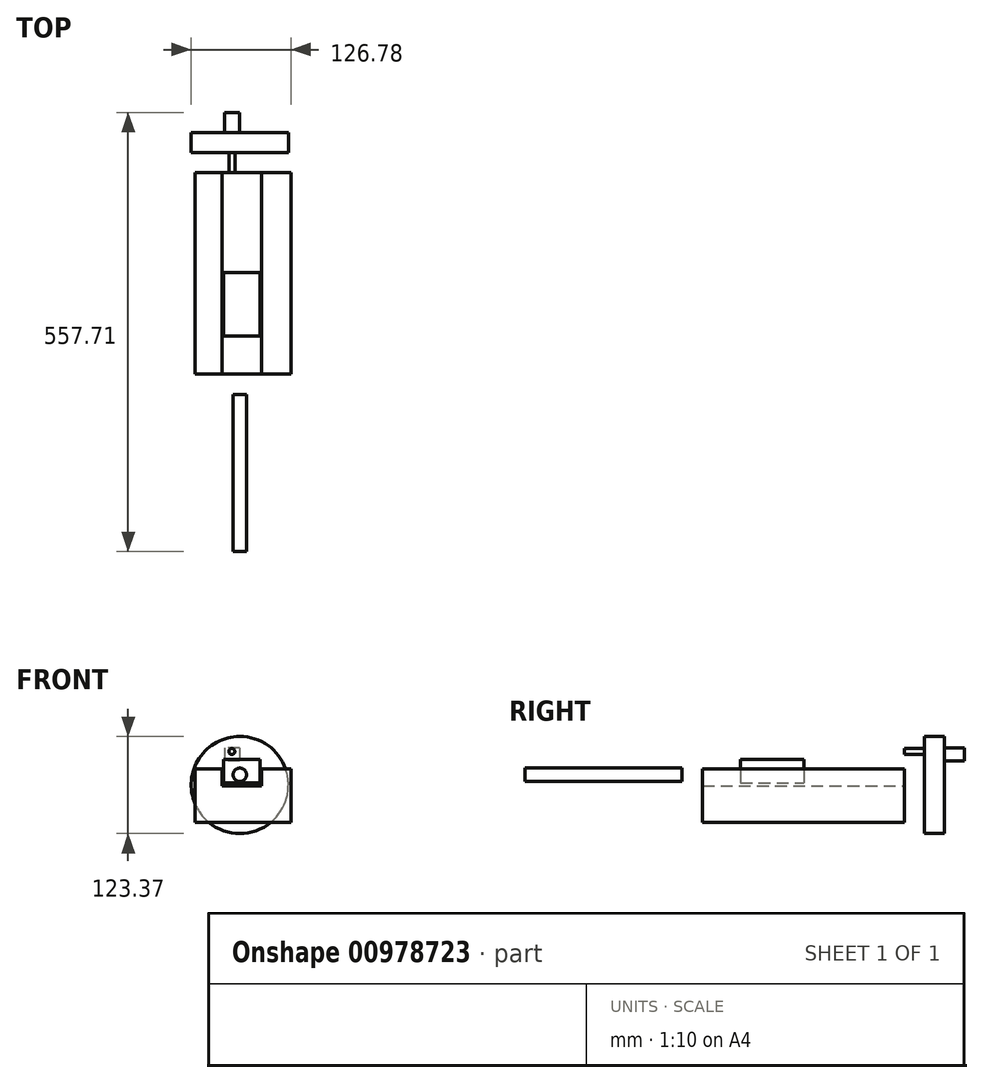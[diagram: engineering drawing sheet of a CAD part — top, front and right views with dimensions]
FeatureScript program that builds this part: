
annotation { "Feature Type Name" : "Feature", "Feature Type Description" : "" }
export const myFeature = defineFeature(function(context is Context, id is Id, definition is map)
    precondition{}
    {
        {
            var Q0;
            Q0=qCreatedBy(makeId("Front.planeOp"),FACE);
            var sketch = newSketch(context, id + "F0", { "sketchPlane" : qUnion([Q0])});
            skLineSegment(sketch, "E0.bottom", {"start": v(-56.8, 36.57) * mm, "end": v(65.1, 36.57) * mm});
            skLineSegment(sketch, "E0.top", {"start": v(-56.8, -30.94) * mm, "end": v(65.1, -30.94) * mm});
            skLineSegment(sketch, "E0.left", {"start": v(-56.8, 36.57) * mm, "end": v(-56.8, -30.94) * mm});
            skLineSegment(sketch, "E0.right", {"start": v(65.1, 36.57) * mm, "end": v(65.1, -30.94) * mm});
            skLineSegment(sketch, "E1.bottom", {"start": v(-22.23, 36.62) * mm, "end": v(27.71, 36.62) * mm});
            skLineSegment(sketch, "E1.top", {"start": v(-22.23, 15.2) * mm, "end": v(27.71, 15.2) * mm});
            skLineSegment(sketch, "E1.left", {"start": v(-22.23, 36.62) * mm, "end": v(-22.23, 15.2) * mm});
            skLineSegment(sketch, "E1.right", {"start": v(27.71, 36.62) * mm, "end": v(27.71, 15.2) * mm});
            skSolve(sketch);
        }
        {
            var Q0;
            Q0=makeQuery(id+"F0.imprint","IMPRINT",FACE,{"disambiguationData":[TD([[makeQuery(id+"F0.imprint","IMPRINT",EDGE,{"derivedFrom":sQuery(id+"F0.wireOp",EDGE,"E0.top")}),1.0]])]});
            extrude(context, id + "F1", {"entities" : qUnion([Q0]), "depth" : 128.76 * mm, "offsetDistance" : 25.4 * mm});
        }
        {
            var Q0;
            Q0=makeQuery(id+"F1.opExtrude","CAP_FACE",FACE,{"disambiguationData":[OSD([sQuery(id+"F0.wireOp",EDGE,"E0.bottom"),sQuery(id+"F0.wireOp",EDGE,"E0.top"),sQuery(id+"F0.wireOp",EDGE,"E0.left"),sQuery(id+"F0.wireOp",EDGE,"E0.right"),sQuery(id+"F0.wireOp",EDGE,"E1.top"),sQuery(id+"F0.wireOp",EDGE,"E1.left"),sQuery(id+"F0.wireOp",EDGE,"E1.right")])],"isStart":true});
            extrude(context, id + "F2", {"entities" : qUnion([Q0]), "operationType" : NewBodyOperationType.ADD, "depth" : 127.3 * mm, "offsetDistance" : 25.4 * mm});
        }
        {
            var Q0;
            Q0=qCreatedBy(makeId("Front.planeOp"),FACE);
            var sketch = newSketch(context, id + "F3", { "sketchPlane" : qUnion([Q0])});
            skLineSegment(sketch, "E2.bottom", {"start": v(-20.3, 48.98) * mm, "end": v(25.66, 48.98) * mm});
            skLineSegment(sketch, "E2.top", {"start": v(-20.3, 18.7) * mm, "end": v(25.66, 18.7) * mm});
            skLineSegment(sketch, "E2.left", {"start": v(-20.3, 48.98) * mm, "end": v(-20.3, 18.7) * mm});
            skLineSegment(sketch, "E2.right", {"start": v(25.66, 48.98) * mm, "end": v(25.66, 18.7) * mm});
            skSolve(sketch);
        }
        {
            var Q0;
            Q0=makeQuery(id+"F3.imprint","IMPRINT",FACE,{"disambiguationData":[TD([[makeQuery(id+"F3.imprint","IMPRINT",EDGE,{"derivedFrom":sQuery(id+"F3.wireOp",EDGE,"E2.bottom")}),-1.0]])]});
            extrude(context, id + "F4", {"entities" : qUnion([Q0]), "depth" : 80.65 * mm, "offsetDistance" : 25.4 * mm});
        }
        {
            var Q0;
            Q0=makeQuery(id+"F4.opExtrude","CAP_FACE",FACE,{"disambiguationData":[OSD([sQuery(id+"F3.wireOp",EDGE,"E2.bottom"),sQuery(id+"F3.wireOp",EDGE,"E2.top"),sQuery(id+"F3.wireOp",EDGE,"E2.left"),sQuery(id+"F3.wireOp",EDGE,"E2.right")])],"isStart":false});
            cPlane(context, id + "F5", {"entities" : qUnion([Q0]), "cplaneType" : CPlaneType.OFFSET, "offset" : 74.08 * mm, "width" : 152.4 * mm, "height" : 152.4 * mm});
        }
        {
            var Q0;
            Q0=qCreatedBy(id+"F5.planeOp",FACE);
            var sketch = newSketch(context, id + "F6", { "sketchPlane" : qUnion([Q0])});
            skCircle(sketch, "E3", {"center": v(0, 29.28) * mm, "radius": 8.49 * mm});
            skSolve(sketch);
        }
        {
            var Q0;
            Q0=makeQuery(id+"F6.imprint","IMPRINT",FACE,{"disambiguationData":[TD([[makeQuery(id+"F6.imprint","IMPRINT",EDGE,{"derivedFrom":sQuery(id+"F6.wireOp",EDGE,"E3")}),1.0]])]});
            extrude(context, id + "F7", {"entities" : qUnion([Q0]), "depth" : 199.5 * mm, "offsetDistance" : 25.4 * mm});
        }
        {
            var Q0;
            Q0=makeQuery(id+"F2.opExtrude","CAP_FACE",FACE,{"disambiguationData":[OSD([sQuery(id+"F0.wireOp",EDGE,"E0.bottom"),sQuery(id+"F0.wireOp",EDGE,"E0.top"),sQuery(id+"F0.wireOp",EDGE,"E0.left"),sQuery(id+"F0.wireOp",EDGE,"E0.right"),sQuery(id+"F0.wireOp",EDGE,"E1.top"),sQuery(id+"F0.wireOp",EDGE,"E1.left"),sQuery(id+"F0.wireOp",EDGE,"E1.right")])],"isStart":false});
            cPlane(context, id + "F8", {"entities" : qUnion([Q0]), "cplaneType" : CPlaneType.OFFSET, "offset" : 25.4 * mm, "width" : 152.4 * mm, "height" : 152.4 * mm});
        }
        {
            var Q0;
            Q0=qCreatedBy(id+"F8.planeOp",FACE);
            var sketch = newSketch(context, id + "F9", { "sketchPlane" : qUnion([Q0])});
            skCircle(sketch, "E4", {"center": v(0, 16.33) * mm, "radius": 61.68 * mm});
            skSolve(sketch);
        }
        {
            var Q0;
            Q0=makeQuery(id+"F9.imprint","IMPRINT",FACE,{"disambiguationData":[TD([[makeQuery(id+"F9.imprint","IMPRINT",EDGE,{"derivedFrom":sQuery(id+"F9.wireOp",EDGE,"E4")}),1.0]])]});
            extrude(context, id + "F10", {"entities" : qUnion([Q0]), "depth" : 25.4 * mm, "offsetDistance" : 25.4 * mm});
        }
        {
            var Q0;
            Q0=makeQuery(id+"F10.opExtrude","CAP_FACE",FACE,{"disambiguationData":[OSD([sQuery(id+"F9.wireOp",EDGE,"E4")])],"isStart":false});
            var sketch = newSketch(context, id + "F11", { "sketchPlane" : qUnion([Q0])});
            skLineSegment(sketch, "E5.bottom", {"start": v(0, 63.46) * mm, "end": v(19.43, 63.46) * mm});
            skLineSegment(sketch, "E5.top", {"start": v(0, 47.01) * mm, "end": v(19.43, 47.01) * mm});
            skLineSegment(sketch, "E5.left", {"start": v(0, 63.46) * mm, "end": v(0, 47.01) * mm});
            skLineSegment(sketch, "E5.right", {"start": v(19.43, 63.46) * mm, "end": v(19.43, 47.01) * mm});
            skSolve(sketch);
        }
        {
            var Q0;
            Q0=makeQuery(id+"F11.imprint","IMPRINT",FACE,{"disambiguationData":[TD([[makeQuery(id+"F11.imprint","IMPRINT",EDGE,{"derivedFrom":sQuery(id+"F11.wireOp",EDGE,"E5.bottom")}),-1.0]])]});
            extrude(context, id + "F12", {"entities" : qUnion([Q0]), "operationType" : NewBodyOperationType.ADD, "depth" : 25.4 * mm, "offsetDistance" : 25.4 * mm});
        }
        {
            var Q0;
            Q0=makeQuery(id+"F10.opExtrude","CAP_FACE",FACE,{"disambiguationData":[OSD([sQuery(id+"F9.wireOp",EDGE,"E4")])],"isStart":true});
            var sketch = newSketch(context, id + "F13", { "sketchPlane" : qUnion([Q0])});
            skCircle(sketch, "E6", {"center": v(-10.08, 58.85) * mm, "radius": 3.8 * mm});
            skSolve(sketch);
        }
        {
            var Q0;
            Q0=makeQuery(id+"F13.imprint","IMPRINT",FACE,{"disambiguationData":[TD([[makeQuery(id+"F13.imprint","IMPRINT",EDGE,{"derivedFrom":sQuery(id+"F13.wireOp",EDGE,"E6")}),1.0]])]});
            extrude(context, id + "F14", {"entities" : qUnion([Q0]), "operationType" : NewBodyOperationType.ADD, "depth" : 25.4 * mm, "offsetDistance" : 25.4 * mm});
        }
    });
